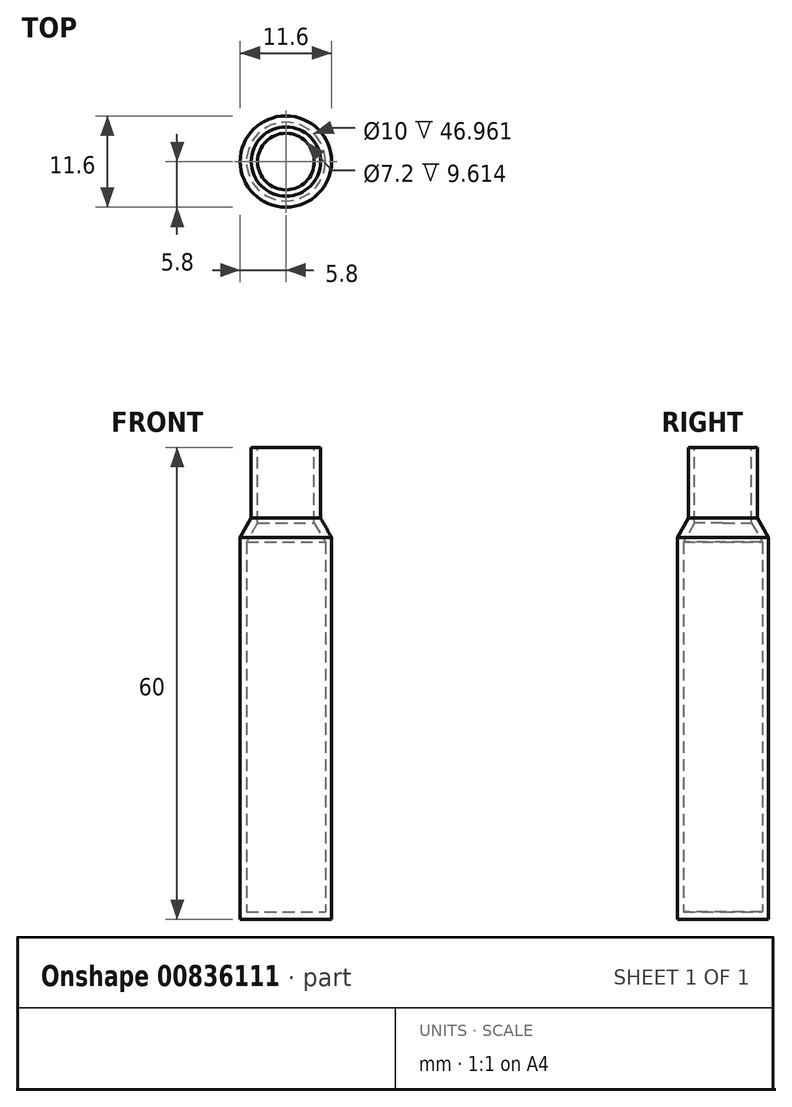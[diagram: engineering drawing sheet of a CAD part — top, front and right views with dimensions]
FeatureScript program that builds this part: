
annotation { "Feature Type Name" : "Feature", "Feature Type Description" : "" }
export const myFeature = defineFeature(function(context is Context, id is Id, definition is map)
    precondition{}
    {
        {
            var Q0;
            Q0=qCreatedBy(makeId("Front.planeOp"),FACE);
            var sketch = newSketch(context, id + "F0", { "sketchPlane" : qUnion([Q0])});
            skLineSegment(sketch, "E0", {"start": v(0, 66.26) * mm, "end": v(0, -66.56) * mm, "construction": true});
            skLineSegment(sketch, "E1", {"start": v(0, 0) * mm, "end": v(5.8, 0) * mm});
            skLineSegment(sketch, "E2", {"start": v(5.8, 0) * mm, "end": v(5.8, 51) * mm});
            skLineSegment(sketch, "E3", {"start": v(5.8, 51) * mm, "end": v(4.4, 51) * mm});
            skLineSegment(sketch, "E4", {"start": v(4.4, 51) * mm, "end": v(4.4, 60) * mm});
            skLineSegment(sketch, "E5", {"start": v(4.4, 60) * mm, "end": v(0, 60) * mm});
            skLineSegment(sketch, "E6", {"start": v(0, 60) * mm, "end": v(0, 0) * mm});
            skLineSegment(sketch, "E7", {"start": v(4.4, 51) * mm, "end": v(5.8, 48.58) * mm});
            skSolve(sketch);
        }
        {
            var Q0;
            {var subQ1=sQuery(id+"F0.wireOp",EDGE,"E1");Q0=makeQuery(id+"F0.imprint","IMPRINT",FACE,{"disambiguationData":[TD([[makeQuery(id+"F0.imprint","IMPRINT",EDGE,{"derivedFrom":subQ1}),1.0]])]});}
            var Q1;
            Q1=sQuery(id+"F0.wireOp",EDGE,"E0");
            revolve(context, id + "F1", {"surfaceOperationType" : NewSurfaceOperationType.NEW, "entities" : qUnion([Q0]), "axis" : qUnion([Q1]), "revolveType" : RevolveType.FULL});
        }
        {
            var Q0;
            Q0=makeQuery(id+"F1.opRevolve","SWEPT_FACE",FACE,{"disambiguationData":[OSD([sQuery(id+"F0.wireOp",EDGE,"E1")])]});
            cPlane(context, id + "F2", {"entities" : qUnion([Q0]), "cplaneType" : CPlaneType.OFFSET, "offset" : 1 * mm, "oppositeDirection" : true, "width" : 150 * mm, "height" : 150 * mm});
        }
        {
            var Q0;
            Q0=qCreatedBy(id+"F2.planeOp",FACE);
            var sketch = newSketch(context, id + "F3", { "sketchPlane" : qUnion([Q0])});
            skCircle(sketch, "E8.0", {"center": v(0, 0) * mm, "radius": 5 * mm});
            skSolve(sketch);
        }
        {
            var Q0;
            Q0 = qSketchRegion(id + "F3", true);
            var Q1;
            Q1=makeQuery(id+"F1.opRevolve","SWEPT_FACE",FACE,{"disambiguationData":[OSD([sQuery(id+"F0.wireOp",EDGE,"E7")])]});
            extrude(context, id + "F4", {"entities" : qUnion([Q0]), "operationType" : NewBodyOperationType.REMOVE, "endBound" : BoundingType.UP_TO_SURFACE, "oppositeDirection" : true, "depth" : 25 * mm, "endBoundEntityFace" : qUnion([Q1]), "hasOffset" : true, "offsetDistance" : 2 * mm});
        }
        {
            var Q0;
            Q0=makeQuery(id+"F1.opRevolve","SWEPT_FACE",FACE,{"disambiguationData":[OSD([sQuery(id+"F0.wireOp",EDGE,"E5")])]});
            var sketch = newSketch(context, id + "F5", { "sketchPlane" : qUnion([Q0])});
            skCircle(sketch, "E9.0", {"center": v(0, 0) * mm, "radius": 3.6 * mm});
            skSolve(sketch);
        }
        {
            var Q0;
            Q0 = qSketchRegion(id + "F5", true);
            var Q1;
            Q1=makeQuery(id+"F1.opRevolve","SWEPT_FACE",FACE,{"disambiguationData":[OSD([sQuery(id+"F0.wireOp",EDGE,"E7")])]});
            extrude(context, id + "F6", {"entities" : qUnion([Q0]), "operationType" : NewBodyOperationType.REMOVE, "endBound" : BoundingType.UP_TO_NEXT, "oppositeDirection" : true, "depth" : 25 * mm, "endBoundEntityFace" : qUnion([Q1]), "offsetDistance" : 25 * mm});
        }
    });
